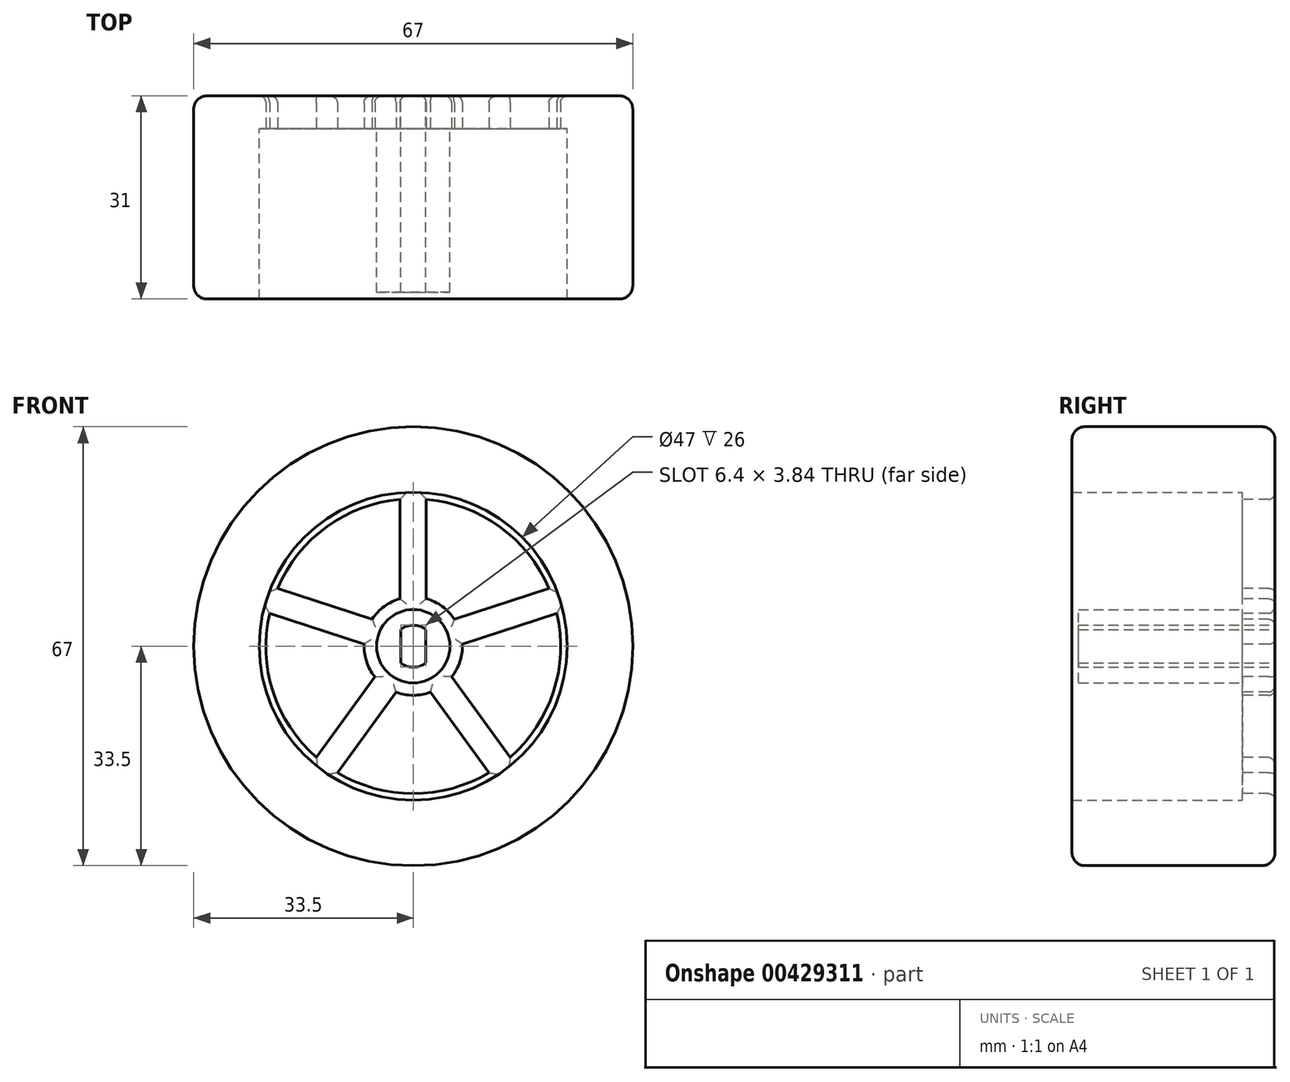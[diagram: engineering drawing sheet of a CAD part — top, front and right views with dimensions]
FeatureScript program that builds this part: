
annotation { "Feature Type Name" : "Feature", "Feature Type Description" : "" }
export const myFeature = defineFeature(function(context is Context, id is Id, definition is map)
    precondition{}
    {
        {
            var Q0;
            Q0=qCreatedBy(makeId("Front.planeOp"),FACE);
            var sketch = newSketch(context, id + "F0", { "sketchPlane" : qUnion([Q0])});
            skCircle(sketch, "E0", {"center": v(0, 0) * mm, "radius": 1 * mm});
            skCircle(sketch, "E1", {"center": v(0, 0) * mm, "radius": 3.2 * mm});
            skLineSegment(sketch, "E2", {"start": v(-1.92, 4.6) * mm, "end": v(-1.92, -5.03) * mm, "construction": true});
            skLineSegment(sketch, "E3.MirrorCS", {"start": v(1.92, 4.6) * mm, "end": v(1.92, -5.03) * mm, "construction": true});
            skLineSegment(sketch, "E4", {"start": v(-1.92, 2.56) * mm, "end": v(-1.92, -2.56) * mm});
            skLineSegment(sketch, "E5", {"start": v(1.92, -2.56) * mm, "end": v(1.92, 2.56) * mm});
            skCircle(sketch, "E6", {"center": v(0, 0) * mm, "radius": 5.6 * mm});
            skSolve(sketch);
        }
        {
            var Q0;
            {var subQ0=sQuery(id+"F0.wireOp",EDGE,"E5");Q0=makeQuery(id+"F0.imprint","IMPRINT",FACE,{"disambiguationData":[TD([[makeQuery(id+"F0.imprint","IMPRINT",EDGE,{"derivedFrom":subQ0}),-1.0]])]});}
            var Q1;
            {var subQ0=sQuery(id+"F0.wireOp",EDGE,"E4");Q1=makeQuery(id+"F0.imprint","IMPRINT",FACE,{"disambiguationData":[TD([[makeQuery(id+"F0.imprint","IMPRINT",EDGE,{"derivedFrom":subQ0}),-1.0]])]});}
            var Q2;
            Q2=makeQuery(id+"F0.imprint","IMPRINT",FACE,{"disambiguationData":[TD([[makeQuery(id+"F0.imprint","IMPRINT",EDGE,{"derivedFrom":sQuery(id+"F0.wireOp",EDGE,"E6")}),1.0]])]});
            extrude(context, id + "F1", {"entities" : qUnion([Q0, Q1, Q2]), "depth" : 25 * mm});
        }
        {
            var Q0;
            Q0=makeQuery(id+"F1.opExtrude","CAP_FACE",FACE,{"disambiguationData":[OSD([sQuery(id+"F0.wireOp",EDGE,"E1"),sQuery(id+"F0.wireOp",EDGE,"E4"),sQuery(id+"F0.wireOp",EDGE,"E5"),sQuery(id+"F0.wireOp",EDGE,"E6")])],"isStart":true});
            var sketch = newSketch(context, id + "F2", { "sketchPlane" : qUnion([Q0])});
            skArc(sketch, "E7", {"start": v(20.7, 8.83) * mm, "mid": v(13.23, 18.2) * mm, "end": v(2, 22.41) * mm});
            skCircle(sketch, "E8", {"center": v(0, 0) * mm, "radius": 33.5 * mm});
            skLineSegment(sketch, "E9", {"start": v(0, 0) * mm, "end": v(0, 3.2) * mm});
            skPoint(sketch, "E9.endSnap0", {"position": v(0, 3.2) * mm});
            skLineSegment(sketch, "E10.0", {"start": v(2, 2.75) * mm, "end": v(2, 22.5) * mm});
            skLineSegment(sketch, "E11.trimOffspring", {"start": v(6.26, 4.14) * mm, "end": v(20.78, 8.85) * mm});
            skPoint(sketch, "E12.orphan", {"position": v(0, 22.5) * mm});
            skLineSegment(sketch, "E13.1.0", {"start": v(-6.26, 4.14) * mm, "end": v(-20.78, 8.85) * mm});
            skArc(sketch, "E13.1.1", {"start": v(-2, 22.41) * mm, "mid": v(-13.23, 18.2) * mm, "end": v(-20.7, 8.83) * mm});
            skLineSegment(sketch, "E13.1.2", {"start": v(-2, 7.23) * mm, "end": v(-2, 22.5) * mm});
            skLineSegment(sketch, "E13.2.0", {"start": v(-5.87, -4.67) * mm, "end": v(-14.84, -17.03) * mm});
            skArc(sketch, "E13.2.1", {"start": v(-21.93, 5.02) * mm, "mid": v(-21.4, -6.95) * mm, "end": v(-14.8, -16.96) * mm});
            skLineSegment(sketch, "E13.2.2", {"start": v(-7.5, 0.33) * mm, "end": v(-22.02, 5.05) * mm});
            skLineSegment(sketch, "E14.1.3.0", {"start": v(2.63, -7.02) * mm, "end": v(11.6, -19.38) * mm});
            skArc(sketch, "E14.3.3.0", {"start": v(-11.55, -19.3) * mm, "mid": v(0, -22.5) * mm, "end": v(11.55, -19.3) * mm});
            skLineSegment(sketch, "E14.7.3.0", {"start": v(-2.63, -7.02) * mm, "end": v(-11.6, -19.38) * mm});
            skLineSegment(sketch, "E14.1.4.0", {"start": v(7.5, 0.33) * mm, "end": v(22.02, 5.05) * mm});
            skArc(sketch, "E14.3.4.0", {"start": v(14.8, -16.96) * mm, "mid": v(21.4, -6.95) * mm, "end": v(21.93, 5.02) * mm});
            skLineSegment(sketch, "E14.7.4.0", {"start": v(5.87, -4.67) * mm, "end": v(14.84, -17.03) * mm});
            skCircle(sketch, "E15", {"center": v(0, 0) * mm, "radius": 7.5 * mm});
            skSolve(sketch);
        }
        {
            var Q0;
            Q0=makeQuery(id+"F2.imprint","IMPRINT",FACE,{"disambiguationData":[TD([[makeQuery(id+"F2.imprint","IMPRINT",EDGE,{"derivedFrom":makeQuery(id+"F1.opExtrude","CAP_EDGE",EDGE,{"disambiguationData":[OSD([sQuery(id+"F0.wireOp",EDGE,"E6")])],"isStart":true})}),1.0]])]});
            var Q1;
            {var subQ11=sQuery(id+"F2.wireOp",EDGE,"E7");Q1=makeQuery(id+"F2.imprint","IMPRINT",FACE,{"disambiguationData":[TD([[makeQuery(id+"F2.imprint","IMPRINT",EDGE,{"derivedFrom":subQ11}),-1.0]])]});}
            var Q2;
            {var subQ2=sQuery(id+"F0.wireOp",EDGE,"E4");var subQ3=makeQuery(id+"F1.opExtrude","CAP_EDGE",EDGE,{"disambiguationData":[OSD([subQ2])],"isStart":true});Q2=makeQuery(id+"F2.imprint","IMPRINT",FACE,{"disambiguationData":[TD([[makeQuery(id+"F2.imprint","IMPRINT",EDGE,{"derivedFrom":subQ3}),1.0]])]});}
            extrude(context, id + "F3", {"entities" : qUnion([Q0, Q1, Q2]), "operationType" : NewBodyOperationType.ADD, "depth" : 5 * mm});
        }
        {
            var Q0;
            Q0=makeQuery(id+"F3.opExtrude","CAP_FACE",FACE,{"disambiguationData":[OSD([sQuery(id+"F0.wireOp",EDGE,"E1"),sQuery(id+"F0.wireOp",EDGE,"E4"),sQuery(id+"F0.wireOp",EDGE,"E5"),sQuery(id+"F2.wireOp",EDGE,"E7"),sQuery(id+"F2.wireOp",EDGE,"E8"),sQuery(id+"F2.wireOp",EDGE,"E10.0"),sQuery(id+"F2.wireOp",EDGE,"E11.trimOffspring"),sQuery(id+"F2.wireOp",EDGE,"E13.1.0"),sQuery(id+"F2.wireOp",EDGE,"E13.1.1"),sQuery(id+"F2.wireOp",EDGE,"E13.1.2"),sQuery(id+"F2.wireOp",EDGE,"E13.2.0"),sQuery(id+"F2.wireOp",EDGE,"E13.2.1"),sQuery(id+"F2.wireOp",EDGE,"E13.2.2"),sQuery(id+"F2.wireOp",EDGE,"E14.1.3.0"),sQuery(id+"F2.wireOp",EDGE,"E14.3.3.0"),sQuery(id+"F2.wireOp",EDGE,"E14.7.3.0"),sQuery(id+"F2.wireOp",EDGE,"E14.1.4.0"),sQuery(id+"F2.wireOp",EDGE,"E14.3.4.0"),sQuery(id+"F2.wireOp",EDGE,"E14.7.4.0"),sQuery(id+"F2.wireOp",EDGE,"E15")])],"isStart":true});
            var sketch = newSketch(context, id + "F4", { "sketchPlane" : qUnion([Q0])});
            skCircle(sketch, "E16.0", {"center": v(0, 0) * mm, "radius": 23.5 * mm});
            skSolve(sketch);
        }
        {
            var Q0;
            Q0=makeQuery(id+"F4.imprint","IMPRINT",FACE,{"disambiguationData":[TD([[makeQuery(id+"F4.imprint","IMPRINT",EDGE,{"derivedFrom":sQuery(id+"F4.wireOp",EDGE,"E16.0")}),-1.0]])]});
            extrude(context, id + "F5", {"entities" : qUnion([Q0]), "operationType" : NewBodyOperationType.ADD, "depth" : 26 * mm});
        }
        {
            var Q0;
            Q0=makeQuery(id+"F3.opExtrude","CAP_EDGE",EDGE,{"disambiguationData":[OSD([sQuery(id+"F2.wireOp",EDGE,"E8")])],"isStart":false});
            var Q1;
            Q1=makeQuery(id+"F5.opExtrude","CAP_EDGE",EDGE,{"disambiguationData":[OSD([sQuery(id+"F2.wireOp",EDGE,"E8")])],"isStart":false});
            fillet(context, id + "F6", {"entities" : qUnion([Q0, Q1]), "radius" : 2 * mm, "tangentPropagation" : true, "allowEdgeOverflow" : false});
        }
        {
            var Q0;
            Q0=makeQuery(id+"F3.opExtrude","CAP_EDGE",EDGE,{"disambiguationData":[OSD([sQuery(id+"F2.wireOp",EDGE,"E13.1.0")])],"isStart":false});
            var Q1;
            Q1=makeQuery(id+"F3.opExtrude","CAP_EDGE",EDGE,{"disambiguationData":[OSD([sQuery(id+"F2.wireOp",EDGE,"E13.1.2")])],"isStart":false});
            var Q2;
            {var subQ0=sQuery(id+"F2.wireOp",EDGE,"E15");Q2=makeQuery(id+"F3.opExtrude","CAP_EDGE",EDGE,{"disambiguationData":[OSD([subQ0]),TDD([makeQuery(id+"F2.imprint","IMPRINT",EDGE,{"disambiguationData":[TD([[makeQuery(id+"F2.imprint","INTERSECT",VERTEX,{"derivedFrom":[sQuery(id+"F2.wireOp",EDGE,"E13.1.0"),subQ0]}),1.0]])],"derivedFrom":subQ0})])],"isStart":false});}
            var Q3;
            Q3=makeQuery(id+"F3.opExtrude","CAP_EDGE",EDGE,{"disambiguationData":[OSD([sQuery(id+"F2.wireOp",EDGE,"E13.1.1")])],"isStart":false});
            var Q4;
            Q4=makeQuery(id+"F3.opExtrude","CAP_EDGE",EDGE,{"disambiguationData":[OSD([sQuery(id+"F2.wireOp",EDGE,"E10.0")])],"isStart":false});
            var Q5;
            Q5=makeQuery(id+"F3.opExtrude","CAP_EDGE",EDGE,{"disambiguationData":[OSD([sQuery(id+"F2.wireOp",EDGE,"E7")])],"isStart":false});
            var Q6;
            Q6=makeQuery(id+"F3.opExtrude","CAP_EDGE",EDGE,{"disambiguationData":[OSD([sQuery(id+"F2.wireOp",EDGE,"E11.trimOffspring")])],"isStart":false});
            var Q7;
            {var subQ0=sQuery(id+"F2.wireOp",EDGE,"E15");Q7=makeQuery(id+"F3.opExtrude","CAP_EDGE",EDGE,{"disambiguationData":[OSD([subQ0]),TDD([makeQuery(id+"F2.imprint","IMPRINT",EDGE,{"disambiguationData":[TD([[makeQuery(id+"F2.imprint","INTERSECT",VERTEX,{"derivedFrom":[sQuery(id+"F2.wireOp",EDGE,"E11.trimOffspring"),subQ0]}),-1.0]])],"derivedFrom":subQ0})])],"isStart":false});}
            var Q8;
            Q8=makeQuery(id+"F3.opExtrude","CAP_EDGE",EDGE,{"disambiguationData":[OSD([sQuery(id+"F2.wireOp",EDGE,"E14.1.4.0")])],"isStart":false});
            var Q9;
            Q9=makeQuery(id+"F3.opExtrude","CAP_EDGE",EDGE,{"disambiguationData":[OSD([sQuery(id+"F2.wireOp",EDGE,"E14.3.4.0")])],"isStart":false});
            var Q10;
            Q10=makeQuery(id+"F3.opExtrude","CAP_EDGE",EDGE,{"disambiguationData":[OSD([sQuery(id+"F2.wireOp",EDGE,"E14.7.4.0")])],"isStart":false});
            var Q11;
            {var subQ0=sQuery(id+"F2.wireOp",EDGE,"E15");Q11=makeQuery(id+"F3.opExtrude","CAP_EDGE",EDGE,{"disambiguationData":[OSD([subQ0]),TDD([makeQuery(id+"F2.imprint","IMPRINT",EDGE,{"disambiguationData":[TD([[makeQuery(id+"F2.imprint","INTERSECT",VERTEX,{"derivedFrom":[sQuery(id+"F2.wireOp",EDGE,"E14.1.4.0"),subQ0]}),1.0]])],"derivedFrom":subQ0})])],"isStart":false});}
            var Q12;
            Q12=makeQuery(id+"F3.opExtrude","CAP_EDGE",EDGE,{"disambiguationData":[OSD([sQuery(id+"F2.wireOp",EDGE,"E13.2.0")])],"isStart":false});
            var Q13;
            {var subQ0=sQuery(id+"F2.wireOp",EDGE,"E15");Q13=makeQuery(id+"F3.opExtrude","CAP_EDGE",EDGE,{"disambiguationData":[OSD([subQ0]),TDD([makeQuery(id+"F2.imprint","IMPRINT",EDGE,{"disambiguationData":[TD([[makeQuery(id+"F2.imprint","INTERSECT",VERTEX,{"derivedFrom":[sQuery(id+"F2.wireOp",EDGE,"E13.2.0"),subQ0]}),1.0]])],"derivedFrom":subQ0})])],"isStart":false});}
            var Q14;
            Q14=makeQuery(id+"F3.opExtrude","CAP_EDGE",EDGE,{"disambiguationData":[OSD([sQuery(id+"F2.wireOp",EDGE,"E13.2.2")])],"isStart":false});
            var Q15;
            Q15=makeQuery(id+"F3.opExtrude","CAP_EDGE",EDGE,{"disambiguationData":[OSD([sQuery(id+"F2.wireOp",EDGE,"E13.2.1")])],"isStart":false});
            var Q16;
            Q16=makeQuery(id+"F3.opExtrude","CAP_EDGE",EDGE,{"disambiguationData":[OSD([sQuery(id+"F2.wireOp",EDGE,"E14.7.3.0")])],"isStart":false});
            var Q17;
            Q17=makeQuery(id+"F3.opExtrude","CAP_EDGE",EDGE,{"disambiguationData":[OSD([sQuery(id+"F2.wireOp",EDGE,"E14.3.3.0")])],"isStart":false});
            var Q18;
            Q18=makeQuery(id+"F3.opExtrude","CAP_EDGE",EDGE,{"disambiguationData":[OSD([sQuery(id+"F2.wireOp",EDGE,"E14.1.3.0")])],"isStart":false});
            var Q19;
            {var subQ0=sQuery(id+"F2.wireOp",EDGE,"E15");Q19=makeQuery(id+"F3.opExtrude","CAP_EDGE",EDGE,{"disambiguationData":[OSD([subQ0]),TDD([makeQuery(id+"F2.imprint","IMPRINT",EDGE,{"disambiguationData":[TD([[makeQuery(id+"F2.imprint","INTERSECT",VERTEX,{"derivedFrom":[sQuery(id+"F2.wireOp",EDGE,"E14.1.3.0"),subQ0]}),1.0]])],"derivedFrom":subQ0})])],"isStart":false});}
            fillet(context, id + "F7", {"entities" : qUnion([Q0, Q1, Q2, Q3, Q4, Q5, Q6, Q7, Q8, Q9, Q10, Q11, Q12, Q13, Q14, Q15, Q16, Q17, Q18, Q19]), "radius" : 1 * mm, "tangentPropagation" : true, "allowEdgeOverflow" : false});
        }
    });
